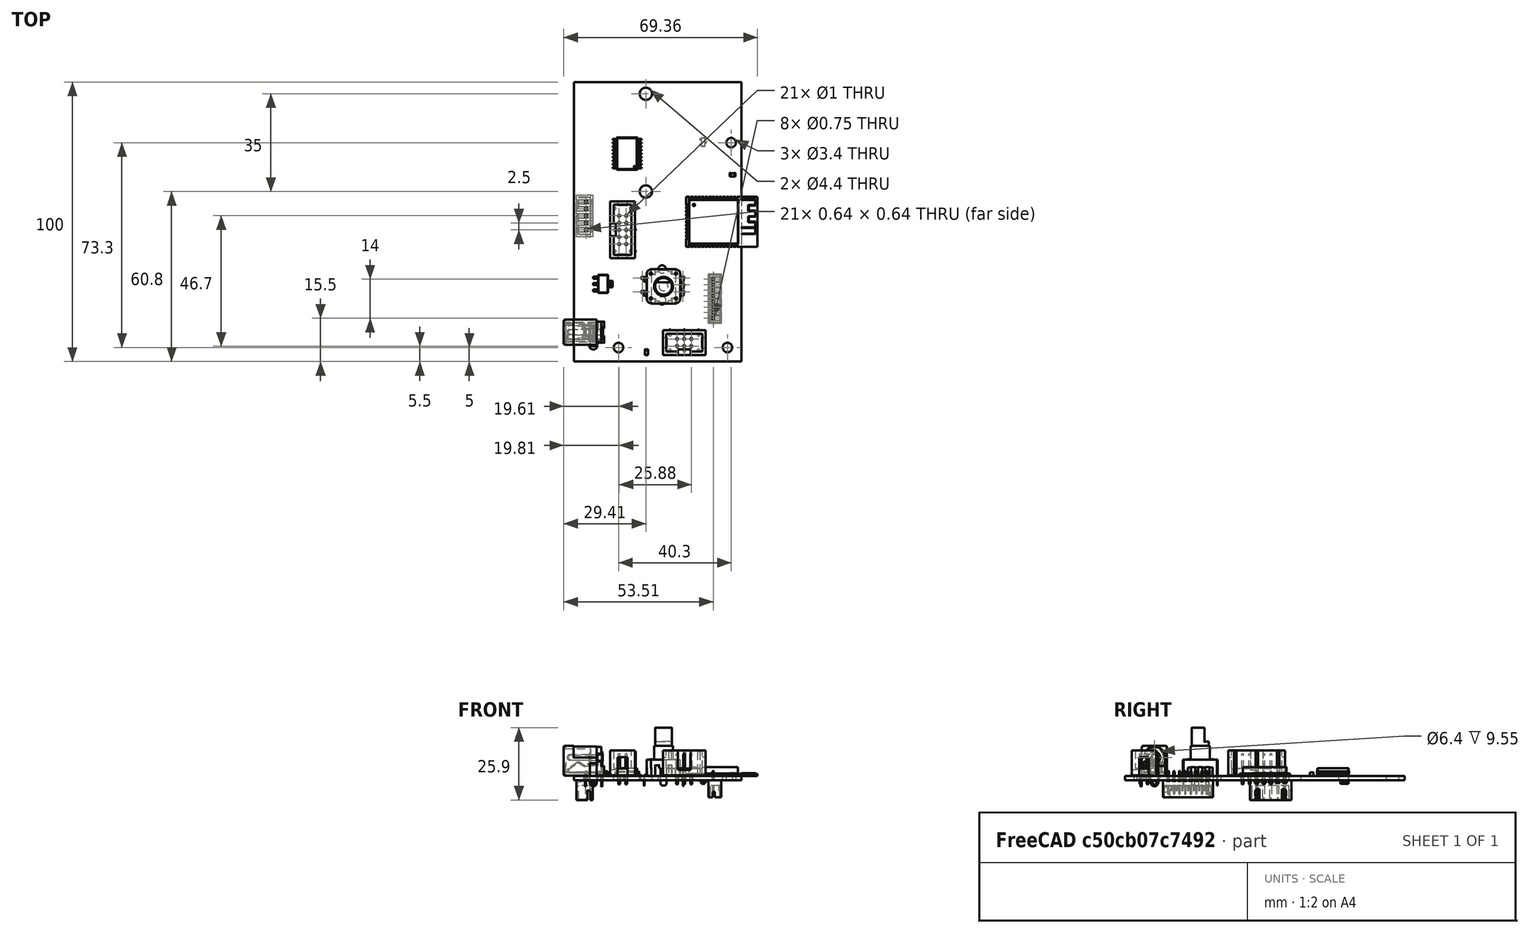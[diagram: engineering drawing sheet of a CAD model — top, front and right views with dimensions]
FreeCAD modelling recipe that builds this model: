
FCSTD DOCUMENT  (FreeCAD 0.19R24291 (Git))
Label: PCB
License: All rights reserved
LicenseURL: http://en.wikipedia.org/wiki/All_rights_reserved
objects: Part::Feature×13, App::Part×5, App::Link×5, PartDesign::CoordinateSystem×3, Sketcher::SketchObject×1
note: 17 computed .brp shape members not serialized (recipe doc carries the construction recipe); baked Part::Feature solids carry a one-line shape summary decoded from their .brp

FEATURE [PartDesign::CoordinateSystem] Local_CS_18fc
  AttacherType = Attacher::AttachEngine3D
FEATURE [Part::Feature] Pcb_18fc
  Placement = pos=(-134.21,133.38,0) rot=(0,0,1;0rad)
  shape: bbox 60 x 100 x 1.6 mm, 67 faces (baked)
FEATURE [Sketcher::SketchObject] PCB_Sketch_18fc
  FullyConstrained = false
  sketch-geometry (9):
    g0: LineSegment StartX=60 StartY=100 StartZ=0 EndX=60 EndY=0 EndZ=0
    g1: LineSegment StartX=60 StartY=0 StartZ=0 EndX=0 EndY=0 EndZ=0
    g2: LineSegment StartX=0 StartY=100 StartZ=0 EndX=60 EndY=100 EndZ=0
    g3: LineSegment StartX=0 StartY=100 StartZ=0 EndX=0 EndY=0 EndZ=0
    g4: Circle CenterX=25.8 CenterY=95.8 CenterZ=0 NormalX=0 NormalY=0 NormalZ=1 AngleXU=0 Radius=2.2
    g5: Circle CenterX=25.8 CenterY=60.8 CenterZ=0 NormalX=0 NormalY=0 NormalZ=1 AngleXU=0 Radius=2.2
    g6: Circle CenterX=56.3 CenterY=78.3 CenterZ=0 NormalX=0 NormalY=0 NormalZ=1 AngleXU=0 Radius=1.7
    g7: Circle CenterX=55 CenterY=5 CenterZ=0 NormalX=0 NormalY=0 NormalZ=1 AngleXU=0 Radius=1.7
    g8: Circle CenterX=16 CenterY=5 CenterZ=0 NormalX=0 NormalY=0 NormalZ=1 AngleXU=0 Radius=1.7
  constraints (4):
    c: Coincident(g3,g1)
    c: Coincident(g2,g3)
    c: Coincident(g0,g1)
    c: Coincident(g2,g0)
FEATURE [App::Part] Board_Geoms_18fc
  Group = -> [Local_CS_18fc,Pcb_18fc,PCB_Sketch_18fc]
  Origin = -> Origin
FEATURE [Part::Feature] Shape  label="J4_JST_B8B_PH_K_61817312"
  Placement = pos=(49.9,29.5,-1.6) rot=(0.707107,-0.707107,0;3.14159rad)
  shape: bbox 4.55 x 17.9 x 9.4 mm, 261 faces (baked)
FEATURE [Part::Feature] Shape001  label="U1_ESP32-WROOM-32_6181740E"
  Placement = pos=(50,50,0) rot=(0,0,-1;1.5708rad)
  shape: bbox 25.5 x 18 x 3.1 mm, 751 faces (baked)
FEATURE [Part::Feature] Shape002  label="J5_JST_B5B_XH_A_61817515"
  Placement = pos=(4.4,47.1,-1.6) rot=(0.707107,0.707107,0;3.14159rad)
  shape: bbox 5.75 x 14.9 x 10.4 mm, 165 faces (baked)
FEATURE [Part::Feature] Shape003  label="U5_SOT_223_61818112"
  Placement = pos=(10.45,27.75,0) rot=(0,0,1;0rad)
  shape: bbox 7 x 6.5 x 1.7 mm, 78 faces (baked)
FEATURE [Part::Feature] Shape004  label="U3_SOT_23_6181763C"
  Placement = pos=(46.3,78.5,-1.6) rot=(1,0,0;3.14159rad)
  shape: bbox 2.5 x 3 x 1.2 mm, 76 faces (baked)
FEATURE [App::Part] Bot_18fc
  Group = -> [Shape,Shape002,Shape004]
  Origin = -> Origin004
FEATURE [Part::Feature] Shape005  label="U2_SOIC_18W_75x116mm_P127mm_6181850D"
  Placement = pos=(19.1,74.4,0) rot=(0,0,1;3.14159rad)
  shape: bbox 10.3 x 11.55 x 2.75 mm, 306 faces (baked)
FEATURE [Part::Feature] Shape006  label="SW2_User Library-PEC12-4220F-S0024-1_61817C63"
  Placement = pos=(32.1,26.9,0) rot=(0.57735,-0.57735,-0.57735;2.0944rad)
  shape: bbox 14.2 x 12.4 x 20.88 mm, 379 faces (baked)
FEATURE [Part::Feature] Shape007  label="R1_R_0805_2012Metric_61817EAB"
  Placement = pos=(26,3.3,0) rot=(0,0,1;1.5708rad)
  shape: bbox 1.2 x 2 x 0.45 mm, 26 faces (baked)
FEATURE [Part::Feature] Shape008  label="J3_BarrelJack_CUI_PJ-202A_Horizontal_7100000000.0"
  Placement = pos=(10,10.5,0) rot=(0,0,1;0rad)
  shape: bbox 14.48 x 9.573 x 14.73 mm, 706 faces, 3 solids (baked)
FEATURE [App::Link] J3_BarrelJack_CUI_PJ_202A_Horizontal_7100000000_0_ln_  label="J3_BarrelJack_CUI_PJ-202A_Horizontal_7100000000.0[2]"
  LinkPlacement = pos=(10,10.5,0) rot=(0,0,1;0rad)
  LinkedObject = -> Shape008
  Placement = pos=(10,10.5,0) rot=(0,0,1;0rad)
FEATURE [Part::Feature] Shape009  label="J2_IDC_Header_2x05_P254mm_Vertical_6181716A"
  Placement = pos=(16.2,52.2,0) rot=(0,0,1;0rad)
  shape: bbox 9.1 x 20.36 x 12.1 mm, 222 faces (baked)
FEATURE [Part::Feature] Shape010  label="J1_IDC_Header_2x03_P254mm_Vertical_61817595"
  Placement = pos=(37,5.5,0) rot=(0,0,1;1.5708rad)
  shape: bbox 15.28 x 9.1 x 12.1 mm, 150 faces (baked)
FEATURE [Part::Feature] Shape011  label="C5_C_0805_2012Metric_61817AE0"
  Placement = pos=(56.8,66.8,0) rot=(0,0,1;0rad)
  shape: bbox 2 x 1.25 x 1.25 mm, 28 faces (baked)
FEATURE [App::Link] C5_C_0805_2012Metric_61817AE0_ln_  label="C4_C_0805_2012Metric_61817AB0"
  LinkPlacement = pos=(56.9,63,0) rot=(0,0,1;0rad)
  LinkedObject = -> Shape011
  Placement = pos=(56.9,63,0) rot=(0,0,1;0rad)
FEATURE [App::Link] C5_C_0805_2012Metric_61817AE0_ln_001  label="C3_C_0805_2012Metric_618180DD"
  LinkPlacement = pos=(12.5,33,0) rot=(0,0,1;3.14159rad)
  LinkedObject = -> Shape011
  Placement = pos=(12.5,33,0) rot=(0,0,1;3.14159rad)
FEATURE [App::Link] C5_C_0805_2012Metric_61817AE0_ln_002  label="C2_C_0805_2012Metric_618180AD"
  LinkPlacement = pos=(8.3375,22.4,0) rot=(0,0,1;0rad)
  LinkedObject = -> Shape011
  Placement = pos=(8.3375,22.4,0) rot=(0,0,1;0rad)
FEATURE [App::Link] C5_C_0805_2012Metric_61817AE0_ln_003  label="C1_C_0805_2012Metric_61817E7B"
  LinkPlacement = pos=(26,9.4625,0) rot=(0,0,1;1.5708rad)
  LinkedObject = -> Shape011
  Placement = pos=(26,9.4625,0) rot=(0,0,1;1.5708rad)
FEATURE [App::Part] Top_18fc
  Group = -> [Shape001,Shape003,Shape005,Shape006,Shape007,Shape008,J3_BarrelJack_CUI_PJ_202A_Horizontal_7100000000_0_ln_,Shape009,Shape010,Shape011,C5_C_0805_2012Metric_61817AE0_ln_,C5_C_0805_2012Metric_61817AE0_ln_001,C5_C_0805_2012Metric_61817AE0_ln_002,C5_C_0805_2012Metric_61817AE0_ln_003]
  Origin = -> Origin003
FEATURE [App::Part] Step_Models_18fc
  Group = -> [Top_18fc,Bot_18fc]
  Origin = -> Origin002
FEATURE [PartDesign::CoordinateSystem] LCS_0  label="LCS_mount1"
  AttacherType = Attacher::AttachEngine3D
  MapMode = 11
  Placement = pos=(16,5,-1.6) rot=(0,0,1;1.5708rad)
  Support = -> [Pcb_18fc]
FEATURE [PartDesign::CoordinateSystem] LCS_knob
  AttacherType = Attacher::AttachEngine3D
  MapMode = 11
  Placement = pos=(32.1,26.9,12.3) rot=(0,0,1;2.15523rad)
  Support = -> [Shape006]
FEATURE [App::Part] Board_18fc  label="PCB"
  Group = -> [Board_Geoms_18fc,Step_Models_18fc,LCS_0,LCS_knob]
  Origin = -> Origin001
